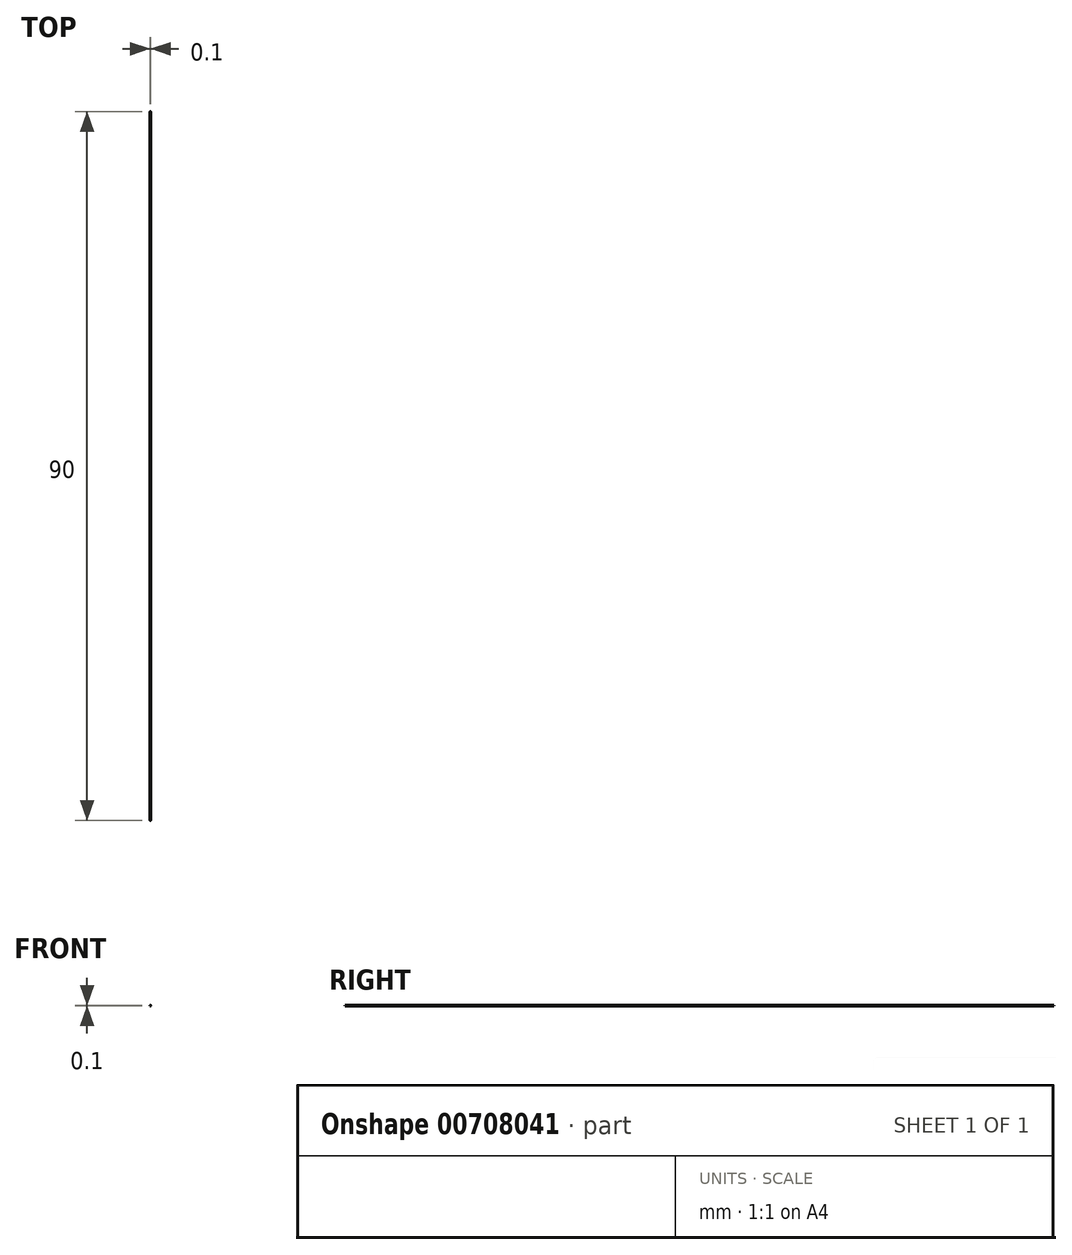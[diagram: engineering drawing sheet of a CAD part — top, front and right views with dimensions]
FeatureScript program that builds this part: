
annotation { "Feature Type Name" : "Feature", "Feature Type Description" : "" }
export const myFeature = defineFeature(function(context is Context, id is Id, definition is map)
    precondition{}
    {
        {
            var Q0;
            Q0=qCreatedBy(makeId("Front.planeOp"),FACE);
            var sketch = newSketch(context, id + "F0", { "sketchPlane" : qUnion([Q0])});
            skCircle(sketch, "E0", {"center": v(0, 0) * mm, "radius": 0.05 * mm});
            skSolve(sketch);
        }
        {
            var Q0;
            Q0 = qSketchRegion(id + "F0", true);
            extrude(context, id + "F1", {"entities" : qUnion([Q0]), "depth" : 90 * mm, "offsetDistance" : 25 * mm});
        }
    });
